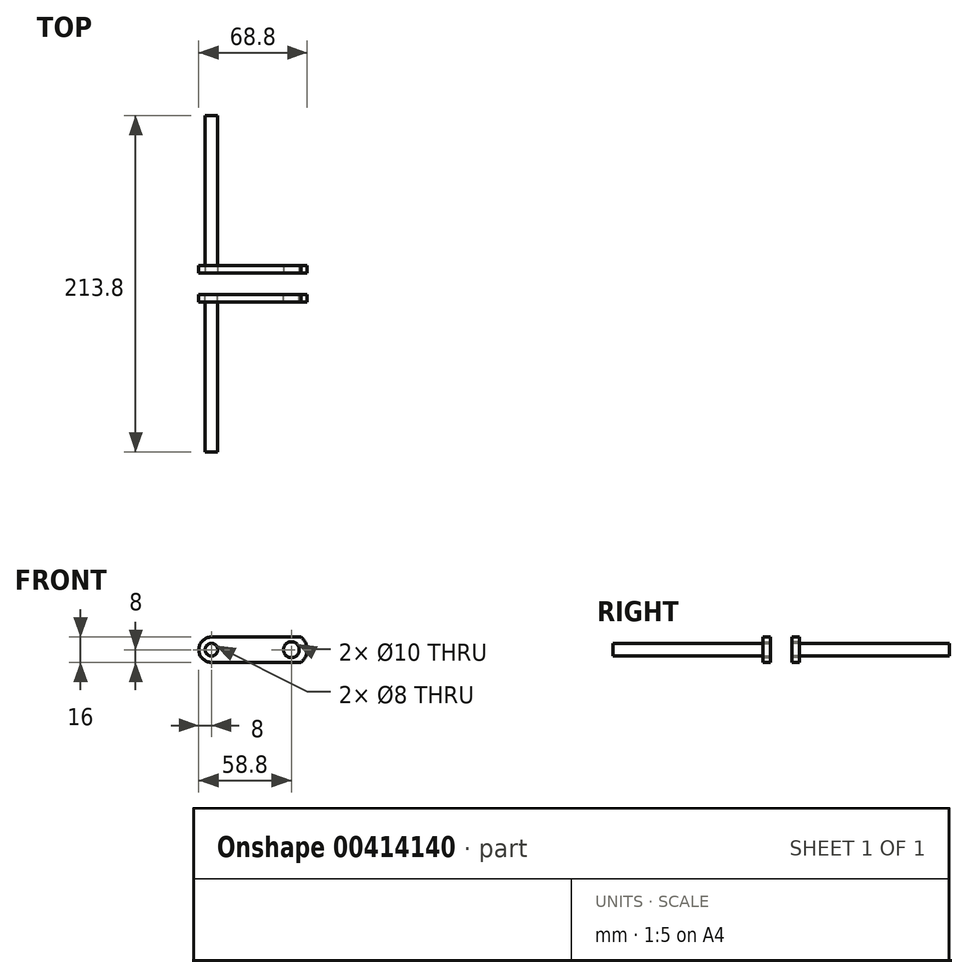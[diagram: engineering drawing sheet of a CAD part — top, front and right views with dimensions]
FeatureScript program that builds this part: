
annotation { "Feature Type Name" : "Feature", "Feature Type Description" : "" }
export const myFeature = defineFeature(function(context is Context, id is Id, definition is map)
    precondition{}
    {
        {
            var Q0;
            Q0=qCreatedBy(makeId("Front.planeOp"),FACE);
            var sketch = newSketch(context, id + "F0", { "sketchPlane" : qUnion([Q0])});
            skCircle(sketch, "E0", {"center": v(0, 0) * mm, "radius": 5 * mm});
            skCircle(sketch, "E1", {"center": v(-50.8, 0) * mm, "radius": 4 * mm});
            skLineSegment(sketch, "E2.bottom", {"start": v(-50.8, 8) * mm, "end": v(6, 8) * mm});
            skLineSegment(sketch, "E2.top", {"start": v(-50.8, -8) * mm, "end": v(6, -8) * mm});
            skLineSegment(sketch, "E3", {"start": v(-50.8, 0) * mm, "end": v(0, 0) * mm, "construction": true});
            skArc(sketch, "E4", {"start": v(-50.8, 8) * mm, "mid": v(-58.8, 0) * mm, "end": v(-50.8, -8) * mm});
            skArc(sketch, "E5", {"start": v(6, 8) * mm, "mid": v(10, 0) * mm, "end": v(6, -8) * mm});
            skSolve(sketch);
        }
        {
            var Q0;
            Q0 = qSketchRegion(id + "F0", true);
            extrude(context, id + "F1", {"entities" : qUnion([Q0]), "depth" : 4.76 * mm});
        }
        {
            var Q0;
            Q0=qCreatedBy(makeId("Front.planeOp"),FACE);
            var sketch = newSketch(context, id + "F2", { "sketchPlane" : qUnion([Q0])});
            skCircle(sketch, "E6.0", {"center": v(-50.8, 0) * mm, "radius": 4 * mm});
            skSolve(sketch);
        }
        {
            var Q0;
            Q0 = qSketchRegion(id + "F2", true);
            extrude(context, id + "F3", {"entities" : qUnion([Q0]), "depth" : 100 * mm});
        }
        {
            var Q0;
            Q0=qCreatedBy(makeId("Front.planeOp"),FACE);
            cPlane(context, id + "F4", {"entities" : qUnion([Q0]), "cplaneType" : CPlaneType.OFFSET, "offset" : 6.9 * mm, "oppositeDirection" : true, "width" : 150 * mm, "height" : 150 * mm});
        }
        {
            var Q0;
            Q0=makeQuery(id+"F1.opExtrude","SWEPT_BODY",BODY,{"disambiguationData":[OSD([sQuery(id+"F0.wireOp",EDGE,"E0"),sQuery(id+"F0.wireOp",EDGE,"E1"),sQuery(id+"F0.wireOp",EDGE,"E2.bottom"),sQuery(id+"F0.wireOp",EDGE,"E2.top"),sQuery(id+"F0.wireOp",EDGE,"E4"),sQuery(id+"F0.wireOp",EDGE,"E5")])]});
            var Q1;
            Q1=makeQuery(id+"F3.opExtrude","SWEPT_BODY",BODY,{"disambiguationData":[OSD([sQuery(id+"F2.wireOp",EDGE,"E6.0")])]});
            var Q2;
            Q2=qCreatedBy(id+"F4.planeOp",FACE);
            mirror(context, id + "F5", {"entities" : qUnion([Q0, Q1]), "mirrorPlane" : qUnion([Q2])});
        }
    });
